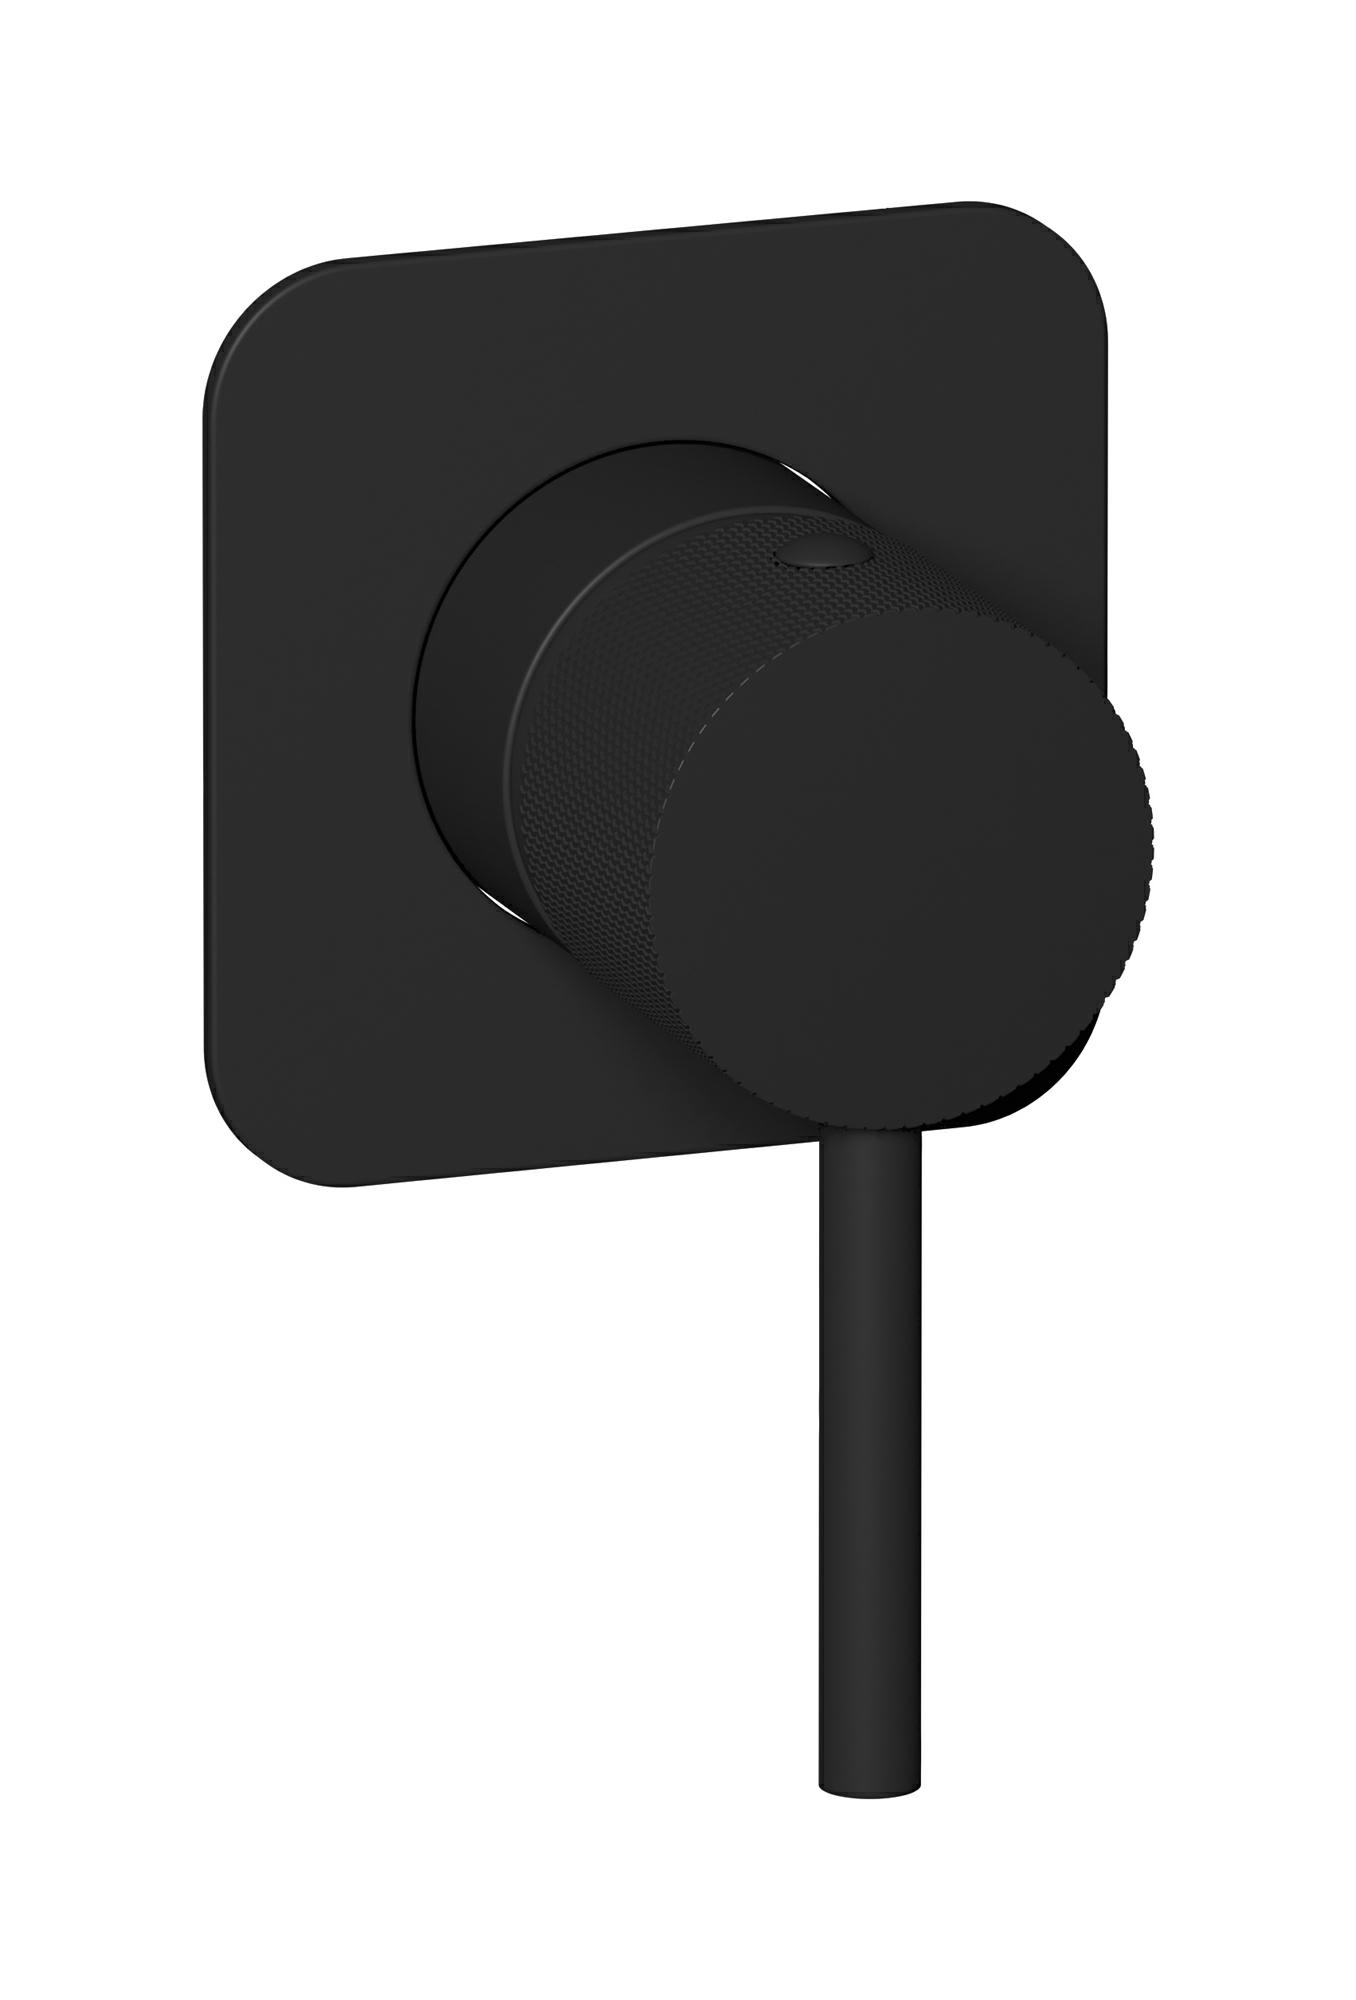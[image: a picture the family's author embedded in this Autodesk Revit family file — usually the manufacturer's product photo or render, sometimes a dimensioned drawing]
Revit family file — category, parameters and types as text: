
# Revit family: ID300
name_source: partatom
category: Apparecchi idraulici
units: mm (PartAtom-declared; Revit-internal decimal feet)

## family parameters
Basato su piano di lavoro = No
Condiviso = No
Mantieni orientamento annotazione = No
Numero OmniClass = 23.45.55.17
Punto di calcolo locali = No
Quota connettore circolare = Usa diametro
Sempre verticale = Sì
Taglio con vuoti quando caricato = No
Tipo di parte = Normale
Titolo OmniClass = Mixing Faucets

## types (12) — shared parameters
Cold water inlet = 10 mm  [stored 0.0328084 ft]
Commenti sul tipo = Wall mixer
Connessione CW = No
Connessione HW = No
Connessione di scarico = No
Connessione di ventilazione = No
Descrizione = Exposed parts for manual wall mixer
Hot water inlet = 10 mm  [stored 0.0328084 ft]
Produttore = IB Rubinetterie S.p.A.
URL = https://www.weareib.it
zero-valued in all types: Prospetto di default

## per-type parameters (varying)
| type | Finishes surface | Immagine tipo | Modello |
| Chrome | IB_Chrome | ID300CC.jpg | ID300CC |
| Brushed nickel | IB_Brushed nickel | ID300SS.jpg | ID300SS |
| Natural brass | IB_Brass | ID300ON.jpg | ID300ON |
| Matt black | IB_matt black | ID300NP.jpg | ID300NP |
| Black chrome | IB_Black chrome | ID300CF.jpg | ID300CF |
| Brushed black chrome | IB_Brushed black chrome | ID300CS.jpg | ID300CS |
| Pale gold | IB_Pale gold | ID300II.jpg | ID300II |
| Brushed pale gold | IB_brushed pale gold | ID300IS.jpg | ID300IS |
| Rose gold | IB_Rose gold | ID300RS.jpg | ID300RS |
| Brushed rose gold | IB_Brushed rose gold | ID300SR.jpg | ID300SR |
| Gold | IB_gold | ID300OO.jpg | ID300OO |
| Brushed gold | IB_brushed gold | ID300OS.jpg | ID300OS |

note: [stored X ft] marks values corroborated as IEEE doubles in the binary element streams (Revit-internal decimal feet)
